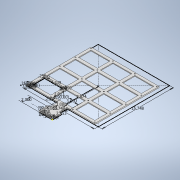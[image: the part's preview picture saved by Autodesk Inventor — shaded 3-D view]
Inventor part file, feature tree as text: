
AUTODESK INVENTOR PART (.ipt)
format: ipt  version: 2020 (Build 240168000, 168)  size: 300,544 bytes
history: native  units: in
note: dims shown in document units (in); Inventor stores cm internally (conversion verified against a paired STEP export)
features: extrude x4, sketch x3, hole x2, pattern_linear x1
ambient origin geometry x8: Origin, YZ Plane, XZ Plane, XY Plane, X Axis, Y Axis, Z Axis, Center Point
bodies: Solid1 (feature_tree)
feature tree (10):
  sketch  "Sketch1"  dims[d0=3.0in d1=2.0in]
  extrude  "Extrusion1"  Depth=2.0in
  hole  "Hole1"  [1 undecoded]
  sketch  "Sketch2"  dims[d2=0.25in d3=1.0in]
  extrude  "Extrusion2"  TaperAngle=0.0deg  [1 undecoded]
  hole  "Hole2"  [1 undecoded]
  extrude  "Extrusion3"  Depth=0.5in
  pattern_linear  "Rectangular Pattern1"  Spacing1=0.25in  [1 undecoded]
  extrude  "Extrusion4"  Depth=0.25in
  sketch  "Sketch3"  dims[d4=1.0in d5=0.0in d6=0.5in d7=0.5in d8=0.25in d9=0.25in d10=2.9528in d11=90.0deg d12=2.9528in d13=1.0in d14=7.874in d15=90.0deg d16=15.748in d17=15.748in d18=0.25in d19=0.0in d20=0.26in d21=0.5in d22=0.375in d23=0.25in d24=0.5635in d25=1.0in d26=0.8108in d27=0.25in d28=90.0deg d29=0.25in d30=0.25in d31=0.25in d32=4.3386in d33=2.9134in d34=0.25in d35=0.25in d36=0.25in d37=0.25in d38=0.25in d39=0.315in d40=90.0deg d41=0.0787in d42=0.0787in d43=0.0787in d44=0.0787in d45=0.0in d46=0.0in d47=0.203in d48=0.625in d49=0.375in d50=0.25in d51=0.5635in d52=1.0in d53=0.8108in d54=0.0787in d55=0.0in d56=1.1811in d58=4.839in d59=1.5748in d61=3.423in d62=0.25in d63=0.25in d64=0.0in d65=0.0in]
note: 4 required parameter values undecoded (feature->parameter linkage not recoverable at this tier; creation-order binding heuristic only, values carry confidence <= 0.55)
